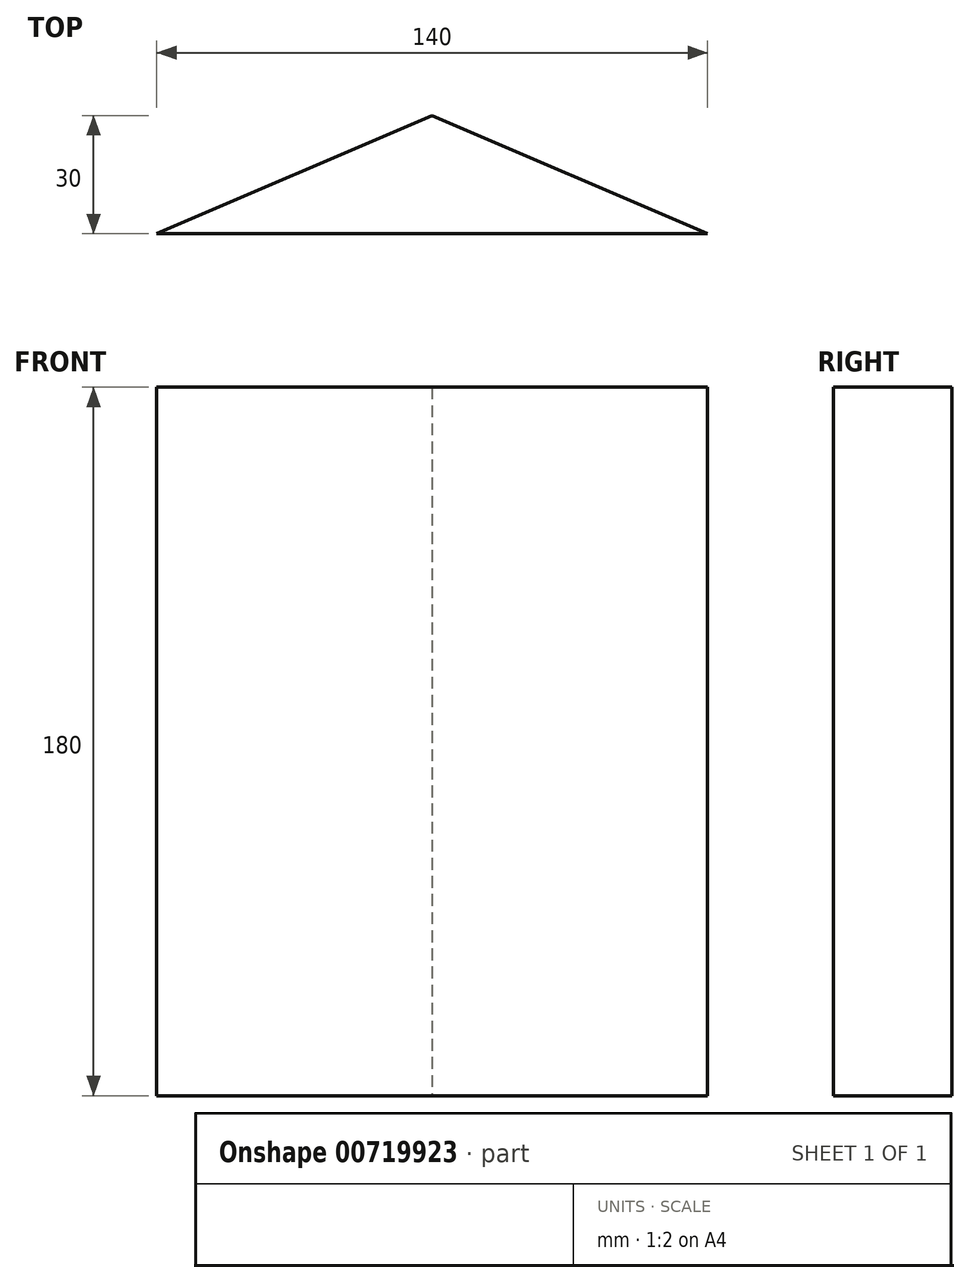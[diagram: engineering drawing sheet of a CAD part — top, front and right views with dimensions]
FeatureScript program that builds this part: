
annotation { "Feature Type Name" : "Feature", "Feature Type Description" : "" }
export const myFeature = defineFeature(function(context is Context, id is Id, definition is map)
    precondition{}
    {
        {
            var Q0;
            Q0=qCreatedBy(makeId("Top.planeOp"),FACE);
            var sketch = newSketch(context, id + "F0", { "sketchPlane" : qUnion([Q0])});
            skLineSegment(sketch, "E0", {"start": v(70, -30) * mm, "end": v(0, 0) * mm});
            skLineSegment(sketch, "E1", {"start": v(-70, -30) * mm, "end": v(0, 0) * mm});
            skLineSegment(sketch, "E2", {"start": v(-70, -30) * mm, "end": v(70, -30) * mm});
            skSolve(sketch);
        }
        {
            var Q0;
            Q0 = qSketchRegion(id + "F0", true);
            extrude(context, id + "F1", {"entities" : qUnion([Q0]), "depth" : 180 * mm, "offsetDistance" : 25 * mm});
        }
    });
